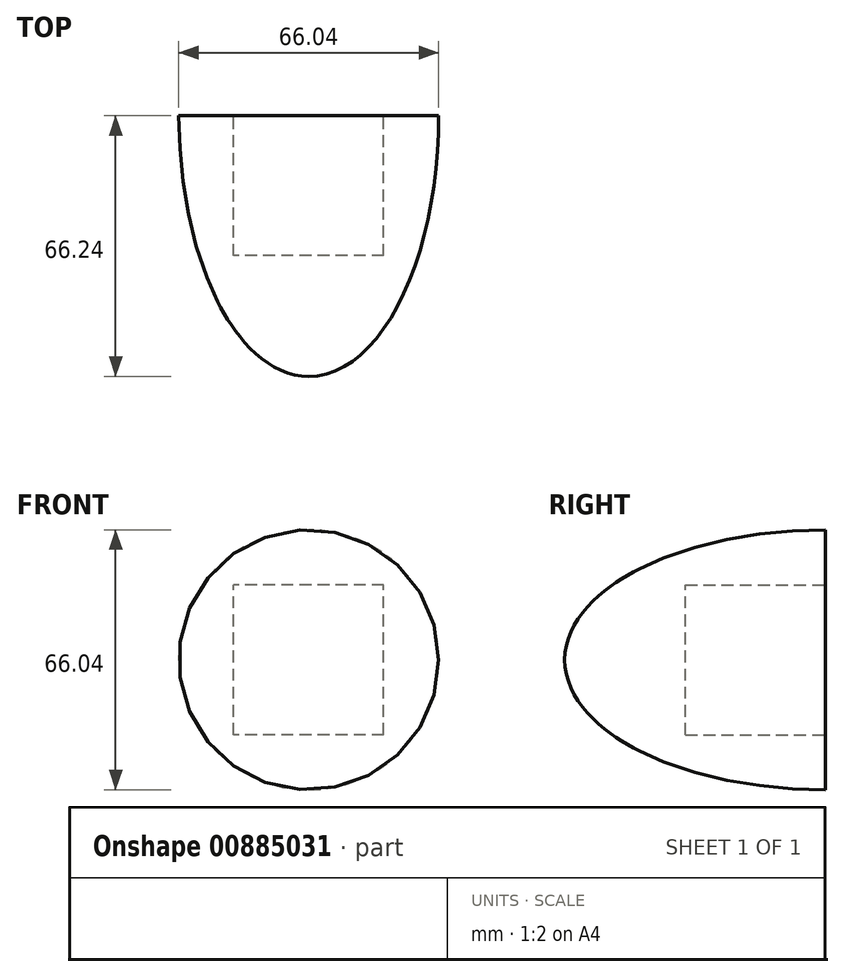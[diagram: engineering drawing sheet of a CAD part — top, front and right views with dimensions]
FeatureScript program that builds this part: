
annotation { "Feature Type Name" : "Feature", "Feature Type Description" : "" }
export const myFeature = defineFeature(function(context is Context, id is Id, definition is map)
    precondition{}
    {
        {
            var Q0;
            Q0=qCreatedBy(makeId("Front.planeOp"),FACE);
            var sketch = newSketch(context, id + "F0", { "sketchPlane" : qUnion([Q0])});
            skLineSegment(sketch, "E0.bottom", {"start": v(19.05, -19.05) * mm, "end": v(-19.05, -19.05) * mm});
            skLineSegment(sketch, "E0.top", {"start": v(19.05, 19.05) * mm, "end": v(-19.05, 19.05) * mm});
            skLineSegment(sketch, "E0.left", {"start": v(19.05, -19.05) * mm, "end": v(19.05, 19.05) * mm});
            skLineSegment(sketch, "E0.right", {"start": v(-19.05, -19.05) * mm, "end": v(-19.05, 19.05) * mm});
            skPoint(sketch, "E0.middle", {"position": v(0, 0) * mm});
            skSolve(sketch);
        }
        {
            var Q0;
            Q0=qCreatedBy(makeId("Top.planeOp"),FACE);
            var sketch = newSketch(context, id + "F1", { "sketchPlane" : qUnion([Q0])});
            skEllipticalArc(sketch, "E1", {});
            skLineSegment(sketch, "E2", {"start": v(-66.11, 0) * mm, "end": v(59.98, 0) * mm});
            skPoint(sketch, "E2.startSnap0", {"position": v(-33.02, 0) * mm});
            skLineSegment(sketch, "E3", {"start": v(0, -66.24) * mm, "end": v(0, 66.24) * mm});
            const initialGuessF1  = {"E1": [0, 0, 0, -1, 0.06623816091230446, 0.03302, 4.71238898038469, 1.5707963267948966]};
            skSetInitialGuess(sketch, initialGuessF1);
            skSolve(sketch);
        }
        {
            var Q0;
            {var subQ0=sQuery(id+"F1.wireOp",EDGE,"E3");var subQ1=sQuery(id+"F1.wireOp",EDGE,"E1");var subQ2=makeQuery(id+"F1.imprint","INTERSECT",VERTEX,{"disambiguationData":[OD(0.0)],"derivedFrom":[subQ1,subQ0]});Q0=makeQuery(id+"F1.imprint","IMPRINT",FACE,{"disambiguationData":[TD([[makeQuery(id+"F1.imprint","IMPRINT",EDGE,{"disambiguationData":[TD([[subQ2,-1.0]])],"derivedFrom":subQ1}),1.0]])]});}
            var Q1;
            Q1=sQuery(id+"F1.wireOp",EDGE,"E3");
            revolve(context, id + "F2", {"surfaceOperationType" : NewSurfaceOperationType.NEW, "entities" : qUnion([Q0]), "axis" : qUnion([Q1]), "revolveType" : RevolveType.FULL});
        }
        {
            var Q0;
            Q0 = qSketchRegion(id + "F0", true);
            extrude(context, id + "F3", {"entities" : qUnion([Q0]), "operationType" : NewBodyOperationType.REMOVE, "depth" : 35.56 * mm, "offsetDistance" : 25.4 * mm});
        }
    });
